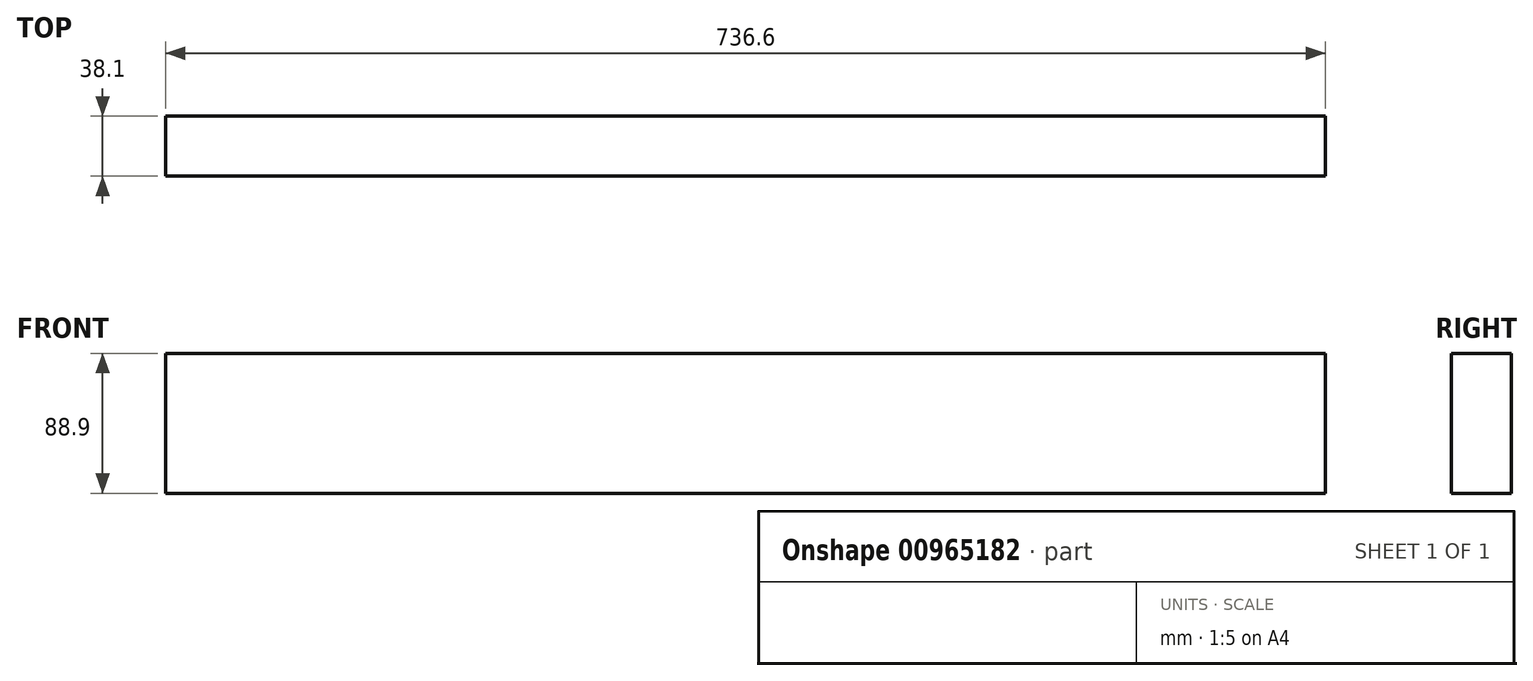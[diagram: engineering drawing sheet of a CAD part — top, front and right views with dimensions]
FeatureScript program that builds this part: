
annotation { "Feature Type Name" : "Feature", "Feature Type Description" : "" }
export const myFeature = defineFeature(function(context is Context, id is Id, definition is map)
    precondition{}
    {
        {
            var Q0;
            Q0=qCreatedBy(makeId("Right.planeOp"),FACE);
            var sketch = newSketch(context, id + "F0", { "sketchPlane" : qUnion([Q0])});
            skLineSegment(sketch, "E0.bottom", {"start": v(190.58, -62.56) * mm, "end": v(228.68, -62.56) * mm});
            skLineSegment(sketch, "E0.top", {"start": v(190.58, 26.34) * mm, "end": v(228.68, 26.34) * mm});
            skLineSegment(sketch, "E0.left", {"start": v(190.58, -62.56) * mm, "end": v(190.58, 26.34) * mm});
            skLineSegment(sketch, "E0.right", {"start": v(228.68, -62.56) * mm, "end": v(228.68, 26.34) * mm});
            skSolve(sketch);
        }
        {
            var Q0;
            Q0=makeQuery(id+"F0.imprint","IMPRINT",FACE,{"disambiguationData":[TD([[makeQuery(id+"F0.imprint","IMPRINT",EDGE,{"derivedFrom":sQuery(id+"F0.wireOp",EDGE,"E0.bottom")}),1.0]])]});
            extrude(context, id + "F1", {"entities" : qUnion([Q0]), "depth" : 736.6 * mm, "offsetDistance" : 25.4 * mm});
        }
    });
